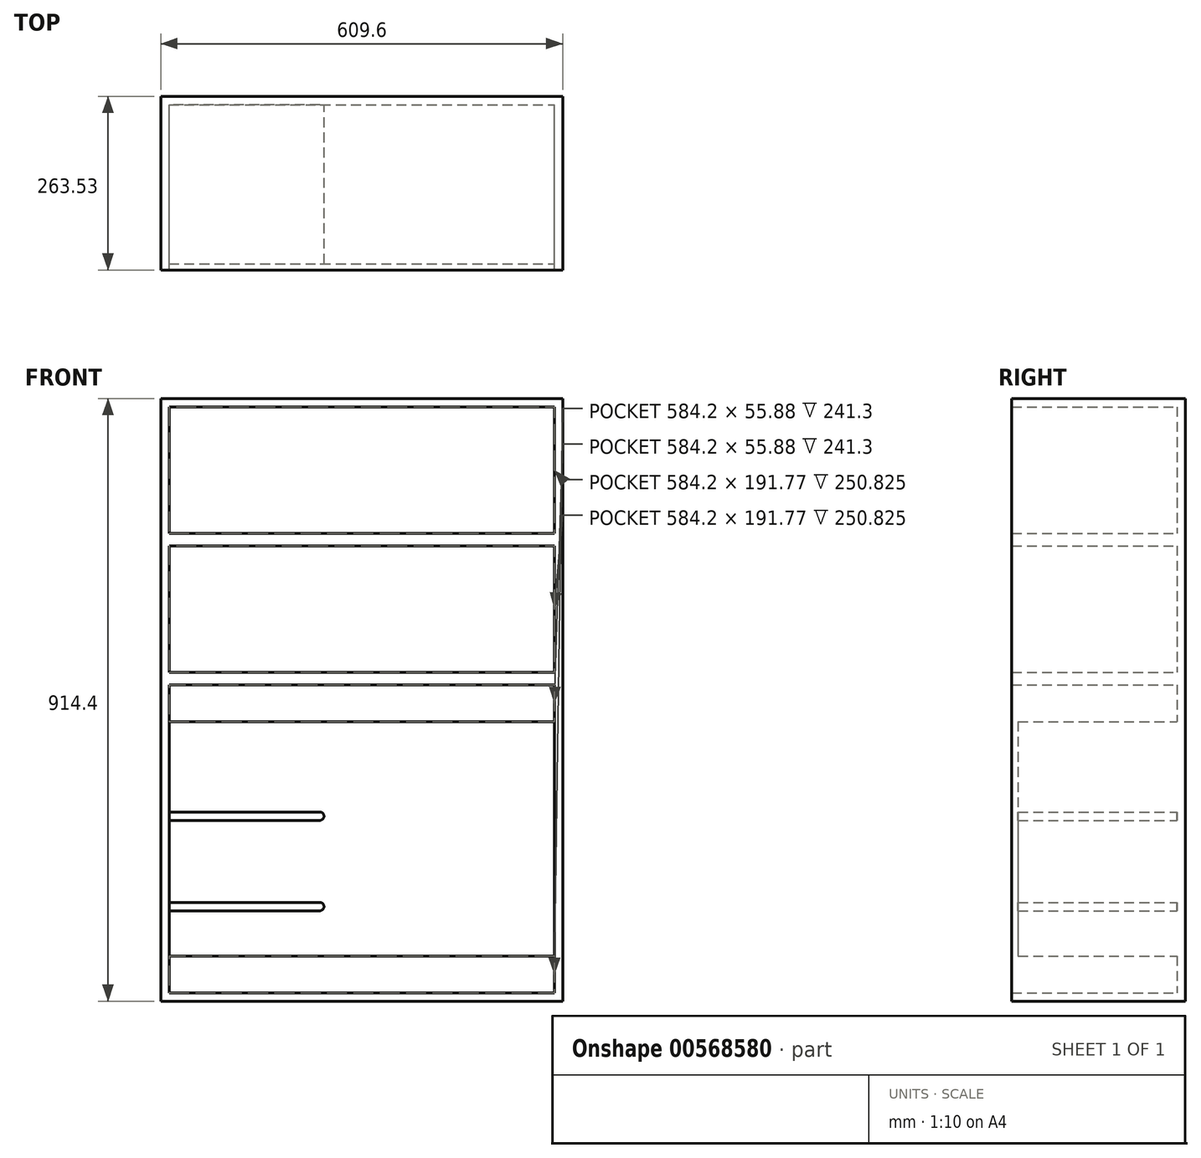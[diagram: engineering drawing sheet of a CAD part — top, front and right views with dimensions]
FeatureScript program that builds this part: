
annotation { "Feature Type Name" : "Feature", "Feature Type Description" : "" }
export const myFeature = defineFeature(function(context is Context, id is Id, definition is map)
    precondition{}
    {
        {
            var Q0;
            Q0=qCreatedBy(makeId("Front.planeOp"),FACE);
            var sketch = newSketch(context, id + "F0", { "sketchPlane" : qUnion([Q0])});
            skLineSegment(sketch, "E0.bottom", {"start": v(304.8, 457.2) * mm, "end": v(-304.8, 457.2) * mm});
            skLineSegment(sketch, "E0.top", {"start": v(304.8, -457.2) * mm, "end": v(-304.8, -457.2) * mm});
            skLineSegment(sketch, "E0.left", {"start": v(304.8, 457.2) * mm, "end": v(304.8, -457.2) * mm});
            skLineSegment(sketch, "E0.right", {"start": v(-304.8, 457.2) * mm, "end": v(-304.8, -457.2) * mm});
            skPoint(sketch, "E0.middle", {"position": v(0, 0) * mm});
            skSolve(sketch);
        }
        {
            var Q0;
            Q0 = qSketchRegion(id + "F0", true);
            extrude(context, id + "F1", {"entities" : qUnion([Q0]), "depth" : 263.52 * mm, "offsetDistance" : 25.4 * mm});
        }
        {
            var Q0;
            Q0=makeQuery(id+"F1.opExtrude","CAP_FACE",FACE,{"disambiguationData":[OSD([sQuery(id+"F0.wireOp",EDGE,"E0.bottom"),sQuery(id+"F0.wireOp",EDGE,"E0.top"),sQuery(id+"F0.wireOp",EDGE,"E0.left"),sQuery(id+"F0.wireOp",EDGE,"E0.right")])],"isStart":false});
            shell(context, id + "F2", {"entities" : qUnion([Q0]), "thickness" : 12.7 * mm});
        }
        {
            var Q0;
            {var subQ0=sQuery(id+"F0.wireOp",EDGE,"E0.bottom");var subQ1=sQuery(id+"F0.wireOp",EDGE,"E0.left");var subQ2=sQuery(id+"F0.wireOp",EDGE,"E0.right");Q0=makeQuery(id+"F2KfqIGzsoq5AxO_1.boolean.opBoolean","SPLIT",FACE,{"disambiguationData":[TD([makeQuery(id+"F2.opShell","OFFSET_FACE",FACE,{"disambiguationData":[OSD([subQ0])]})])],"derivedFrom":makeQuery(id+"F2.opShell","OFFSET_FACE",FACE,{"disambiguationData":[OSD([subQ0,sQuery(id+"F0.wireOp",EDGE,"E0.top"),subQ1,subQ2])]})});}
            var sketch = newSketch(context, id + "F3", { "sketchPlane" : qUnion([Q0])});
            skLineSegment(sketch, "E1.bottom", {"start": v(-292.1, 41.91) * mm, "end": v(292.1, 41.91) * mm});
            skLineSegment(sketch, "E1.top", {"start": v(-292.1, 22.86) * mm, "end": v(292.1, 22.86) * mm});
            skLineSegment(sketch, "E1.left", {"start": v(-292.1, 41.91) * mm, "end": v(-292.1, 22.86) * mm});
            skLineSegment(sketch, "E1.right", {"start": v(292.1, 41.91) * mm, "end": v(292.1, 22.86) * mm});
            skPoint(sketch, "E1.middle", {"position": v(0, 32.39) * mm});
            skLineSegment(sketch, "E2.bottom", {"start": v(-292.1, 252.73) * mm, "end": v(292.1, 252.73) * mm});
            skLineSegment(sketch, "E2.top", {"start": v(-292.1, 233.68) * mm, "end": v(292.1, 233.68) * mm});
            skLineSegment(sketch, "E2.left", {"start": v(-292.1, 252.73) * mm, "end": v(-292.1, 233.68) * mm});
            skLineSegment(sketch, "E2.right", {"start": v(292.1, 252.73) * mm, "end": v(292.1, 233.68) * mm});
            skPoint(sketch, "E2.middle", {"position": v(0, 243.2) * mm});
            skSolve(sketch);
        }
        {
            var Q0;
            Q0 = qSketchRegion(id + "F3", true);
            extrude(context, id + "F4", {"entities" : qUnion([Q0]), "operationType" : NewBodyOperationType.ADD, "depth" : 250.82 * mm, "offsetDistance" : 25.4 * mm});
        }
        {
            var Q0;
            {var subQ0=sQuery(id+"F0.wireOp",EDGE,"E0.top");var subQ1=sQuery(id+"F0.wireOp",EDGE,"E0.left");var subQ2=sQuery(id+"F0.wireOp",EDGE,"E0.right");Q0=makeQuery(id+"F4.boolean.opBoolean","SPLIT",FACE,{"disambiguationData":[TD([makeQuery(id+"F2.opShell","OFFSET_FACE",FACE,{"disambiguationData":[OSD([subQ0])]})])],"derivedFrom":makeQuery(id+"F2.opShell","OFFSET_FACE",FACE,{"disambiguationData":[OSD([sQuery(id+"F0.wireOp",EDGE,"E0.bottom"),subQ0,subQ1,subQ2])]})});}
            var sketch = newSketch(context, id + "F5", { "sketchPlane" : qUnion([Q0])});
            skLineSegment(sketch, "E3", {"start": v(-292.1, -33.02) * mm, "end": v(-63.5, -33.02) * mm});
            skLineSegment(sketch, "E4", {"start": v(-63.5, -45.72) * mm, "end": v(-292.1, -45.72) * mm});
            skLineSegment(sketch, "E5", {"start": v(0, 22.86) * mm, "end": v(0, -444.5) * mm, "construction": true});
            skLineSegment(sketch, "E6.MirrorCS", {"start": v(292.1, -33.02) * mm, "end": v(63.5, -33.02) * mm});
            skLineSegment(sketch, "E7.MirrorCS", {"start": v(63.5, -45.72) * mm, "end": v(292.1, -45.72) * mm});
            skPoint(sketch, "E8.orphan", {"position": v(101.6, -33.02) * mm});
            skPoint(sketch, "E9.MirrorCS.end.orphan", {"position": v(101.6, -45.72) * mm});
            skPoint(sketch, "E10.orphan", {"position": v(-101.6, -33.02) * mm});
            skPoint(sketch, "E11.end.orphan", {"position": v(-101.6, -45.72) * mm});
            skLineSegment(sketch, "E12", {"start": v(292.1, -73.66) * mm, "end": v(-292.1, -73.66) * mm, "construction": true});
            skLineSegment(sketch, "E13.MirrorCS", {"start": v(63.5, -101.6) * mm, "end": v(292.1, -101.6) * mm});
            skLineSegment(sketch, "E14.MirrorCS", {"start": v(292.1, -114.3) * mm, "end": v(63.5, -114.3) * mm});
            skArc(sketch, "E15.MirrorCS", {"start": v(63.5, -114.3) * mm, "mid": v(57.15, -107.95) * mm, "end": v(63.5, -101.6) * mm});
            skLineSegment(sketch, "E16.MirrorCS", {"start": v(-63.5, -101.6) * mm, "end": v(-292.1, -101.6) * mm});
            skLineSegment(sketch, "E17.MirrorCS", {"start": v(-292.1, -114.3) * mm, "end": v(-63.5, -114.3) * mm});
            skArc(sketch, "E18.MirrorCS", {"start": v(-63.5, -114.3) * mm, "mid": v(-57.15, -107.95) * mm, "end": v(-63.5, -101.6) * mm});
            skLineSegment(sketch, "E19", {"start": v(292.1, -142.24) * mm, "end": v(-292.1, -142.24) * mm, "construction": true});
            skLineSegment(sketch, "E20.MirrorCS", {"start": v(292.1, -170.18) * mm, "end": v(63.5, -170.18) * mm});
            skLineSegment(sketch, "E21.MirrorCS", {"start": v(63.5, -182.88) * mm, "end": v(292.1, -182.88) * mm});
            skArc(sketch, "E22.MirrorCS", {"start": v(63.5, -170.18) * mm, "mid": v(57.15, -176.53) * mm, "end": v(63.5, -182.88) * mm});
            skArc(sketch, "E23.MirrorCS", {"start": v(-63.5, -170.18) * mm, "mid": v(-57.15, -176.53) * mm, "end": v(-63.5, -182.88) * mm});
            skLineSegment(sketch, "E24.MirrorCS", {"start": v(-63.5, -182.88) * mm, "end": v(-292.1, -182.88) * mm});
            skLineSegment(sketch, "E25.MirrorCS", {"start": v(-292.1, -170.18) * mm, "end": v(-63.5, -170.18) * mm});
            skLineSegment(sketch, "E26", {"start": v(292.1, -210.82) * mm, "end": v(-292.1, -210.82) * mm, "construction": true});
            skLineSegment(sketch, "E27.MirrorCS", {"start": v(63.5, -238.76) * mm, "end": v(292.1, -238.76) * mm});
            skLineSegment(sketch, "E28.MirrorCS", {"start": v(292.1, -251.46) * mm, "end": v(63.5, -251.46) * mm});
            skArc(sketch, "E29.MirrorCS", {"start": v(63.5, -251.46) * mm, "mid": v(57.15, -245.1) * mm, "end": v(63.5, -238.76) * mm});
            skArc(sketch, "E30.MirrorCS", {"start": v(-63.5, -251.46) * mm, "mid": v(-57.15, -245.11) * mm, "end": v(-63.5, -238.76) * mm});
            skLineSegment(sketch, "E31.MirrorCS", {"start": v(-63.5, -238.76) * mm, "end": v(-292.1, -238.76) * mm});
            skLineSegment(sketch, "E32.MirrorCS", {"start": v(-292.1, -251.46) * mm, "end": v(-63.5, -251.46) * mm});
            skLineSegment(sketch, "E33", {"start": v(292.1, -279.4) * mm, "end": v(-292.1, -279.4) * mm, "construction": true});
            skLineSegment(sketch, "E34.MirrorCS", {"start": v(292.1, -307.34) * mm, "end": v(63.5, -307.34) * mm});
            skLineSegment(sketch, "E35.MirrorCS", {"start": v(63.5, -320.04) * mm, "end": v(292.1, -320.04) * mm});
            skArc(sketch, "E36.MirrorCS", {"start": v(63.5, -307.34) * mm, "mid": v(57.15, -313.7) * mm, "end": v(63.5, -320.04) * mm});
            skArc(sketch, "E37.MirrorCS", {"start": v(-63.5, -307.34) * mm, "mid": v(-57.15, -313.7) * mm, "end": v(-63.5, -320.04) * mm});
            skLineSegment(sketch, "E38.MirrorCS", {"start": v(-63.5, -320.04) * mm, "end": v(-292.1, -320.04) * mm});
            skLineSegment(sketch, "E39.MirrorCS", {"start": v(-292.1, -307.34) * mm, "end": v(-63.5, -307.34) * mm});
            skLineSegment(sketch, "E40", {"start": v(292.1, -347.98) * mm, "end": v(-292.1, -347.98) * mm, "construction": true});
            skLineSegment(sketch, "E41.MirrorCS", {"start": v(63.5, -375.92) * mm, "end": v(292.1, -375.92) * mm});
            skLineSegment(sketch, "E42.MirrorCS", {"start": v(292.1, -388.62) * mm, "end": v(63.5, -388.62) * mm});
            skLineSegment(sketch, "E43.MirrorCS", {"start": v(-63.5, -375.92) * mm, "end": v(-292.1, -375.92) * mm});
            skLineSegment(sketch, "E44.MirrorCS", {"start": v(-292.1, -388.62) * mm, "end": v(-63.5, -388.62) * mm});
            skLineSegment(sketch, "E45", {"start": v(292.1, -416.56) * mm, "end": v(-292.1, -416.56) * mm, "construction": true});
            skLineSegment(sketch, "E46", {"start": v(-63.5, -33.02) * mm, "end": v(63.5, -33.02) * mm});
            skLineSegment(sketch, "E47", {"start": v(-63.5, -45.72) * mm, "end": v(63.5, -45.72) * mm});
            skLineSegment(sketch, "E48", {"start": v(-63.5, -375.92) * mm, "end": v(63.5, -375.92) * mm});
            skLineSegment(sketch, "E49", {"start": v(-63.5, -388.62) * mm, "end": v(63.5, -388.62) * mm});
            skPoint(sketch, "E50.MirrorCS.end.orphan", {"position": v(63.5, -375.92) * mm});
            skPoint(sketch, "E51.MirrorCS.end.orphan", {"position": v(-63.5, -375.92) * mm});
            skPoint(sketch, "E51.MirrorCS.start.orphan", {"position": v(-63.5, -388.62) * mm});
            skSolve(sketch);
        }
        {
            var Q0;
            {var subQ0=sQuery(id+"F5.wireOp",EDGE,"E3");Q0=makeQuery(id+"F5.imprint","IMPRINT",FACE,{"disambiguationData":[TD([[makeQuery(id+"F5.imprint","IMPRINT",EDGE,{"derivedFrom":subQ0}),-1.0]])]});}
            var Q1;
            {var subQ0=sQuery(id+"F5.wireOp",EDGE,"E6.MirrorCS");Q1=makeQuery(id+"F5.imprint","IMPRINT",FACE,{"disambiguationData":[TD([[makeQuery(id+"F5.imprint","IMPRINT",EDGE,{"derivedFrom":subQ0}),1.0]])]});}
            extrude(context, id + "F6", {"entities" : qUnion([Q0, Q1]), "operationType" : NewBodyOperationType.ADD, "depth" : 241.3 * mm, "offsetDistance" : 25.4 * mm});
        }
        {
            var Q0;
            {var subQ0=sQuery(id+"F5.wireOp",EDGE,"E20.MirrorCS");Q0=makeQuery(id+"F5.imprint","IMPRINT",FACE,{"disambiguationData":[TD([[makeQuery(id+"F5.imprint","IMPRINT",EDGE,{"derivedFrom":subQ0}),1.0]])]});}
            var Q1;
            {var subQ0=sQuery(id+"F5.wireOp",EDGE,"E13.MirrorCS");Q1=makeQuery(id+"F5.imprint","IMPRINT",FACE,{"disambiguationData":[TD([[makeQuery(id+"F5.imprint","IMPRINT",EDGE,{"derivedFrom":subQ0}),-1.0]])]});}
            var Q2;
            {var subQ0=sQuery(id+"F5.wireOp",EDGE,"E6.MirrorCS");Q2=makeQuery(id+"F5.imprint","IMPRINT",FACE,{"disambiguationData":[TD([[makeQuery(id+"F5.imprint","IMPRINT",EDGE,{"derivedFrom":subQ0}),1.0]])]});}
            var Q3;
            Q3=makeQuery(id+"F5.imprint","IMPRINT",FACE,{"disambiguationData":[TD([[makeQuery(id+"F5.imprint","IMPRINT",EDGE,{"derivedFrom":sQuery(id+"F5.wireOp",EDGE,"E23.MirrorCS")}),-1.0]])]});
            var Q4;
            {var subQ0=sQuery(id+"F5.wireOp",EDGE,"E16.MirrorCS");Q4=makeQuery(id+"F5.imprint","IMPRINT",FACE,{"disambiguationData":[TD([[makeQuery(id+"F5.imprint","IMPRINT",EDGE,{"derivedFrom":subQ0}),1.0]])]});}
            var Q5;
            {var subQ0=sQuery(id+"F5.wireOp",EDGE,"E3");Q5=makeQuery(id+"F5.imprint","IMPRINT",FACE,{"disambiguationData":[TD([[makeQuery(id+"F5.imprint","IMPRINT",EDGE,{"derivedFrom":subQ0}),-1.0]])]});}
            var Q6;
            Q6=makeQuery(id+"F5.imprint","IMPRINT",FACE,{"disambiguationData":[TD([[makeQuery(id+"F5.imprint","IMPRINT",EDGE,{"derivedFrom":sQuery(id+"F5.wireOp",EDGE,"E30.MirrorCS")}),1.0]])]});
            var Q7;
            {var subQ0=sQuery(id+"F5.wireOp",EDGE,"E27.MirrorCS");Q7=makeQuery(id+"F5.imprint","IMPRINT",FACE,{"disambiguationData":[TD([[makeQuery(id+"F5.imprint","IMPRINT",EDGE,{"derivedFrom":subQ0}),-1.0]])]});}
            var Q8;
            {var subQ0=sQuery(id+"F5.wireOp",EDGE,"E34.MirrorCS");Q8=makeQuery(id+"F5.imprint","IMPRINT",FACE,{"disambiguationData":[TD([[makeQuery(id+"F5.imprint","IMPRINT",EDGE,{"derivedFrom":subQ0}),1.0]])]});}
            var Q9;
            Q9=makeQuery(id+"F5.imprint","IMPRINT",FACE,{"disambiguationData":[TD([[makeQuery(id+"F5.imprint","IMPRINT",EDGE,{"derivedFrom":sQuery(id+"F5.wireOp",EDGE,"E37.MirrorCS")}),-1.0]])]});
            var Q10;
            {var subQ0=sQuery(id+"F5.wireOp",EDGE,"E43.MirrorCS");Q10=makeQuery(id+"F5.imprint","IMPRINT",FACE,{"disambiguationData":[TD([[makeQuery(id+"F5.imprint","IMPRINT",EDGE,{"derivedFrom":subQ0}),1.0]])]});}
            var Q11;
            {var subQ0=sQuery(id+"F5.wireOp",EDGE,"E41.MirrorCS");Q11=makeQuery(id+"F5.imprint","IMPRINT",FACE,{"disambiguationData":[TD([[makeQuery(id+"F5.imprint","IMPRINT",EDGE,{"derivedFrom":subQ0}),-1.0]])]});}
            var Q12;
            Q12=makeQuery(id+"F5.imprint","IMPRINT",FACE,{"disambiguationData":[TD([[makeQuery(id+"F5.imprint","IMPRINT",EDGE,{"derivedFrom":sQuery(id+"F5.wireOp",EDGE,"38393d3f-58ba-4691-93c4-d296c3498af30.MirrorCS")}),-1.0]])]});
            var Q13;
            {var subQ0=sQuery(id+"F5.wireOp",EDGE,"93d55c71-d1c5-40e0-8db1-9db6ebcf69c20.MirrorCS");Q13=makeQuery(id+"F5.imprint","IMPRINT",FACE,{"disambiguationData":[TD([[makeQuery(id+"F5.imprint","IMPRINT",EDGE,{"derivedFrom":subQ0}),1.0]])]});}
            extrude(context, id + "F7", {"entities" : qUnion([Q0, Q1, Q2, Q3, Q4, Q5, Q6, Q7, Q8, Q9, Q10, Q11, Q12, Q13]), "operationType" : NewBodyOperationType.ADD, "depth" : 241.3 * mm, "offsetDistance" : 25.4 * mm});
        }
    });
